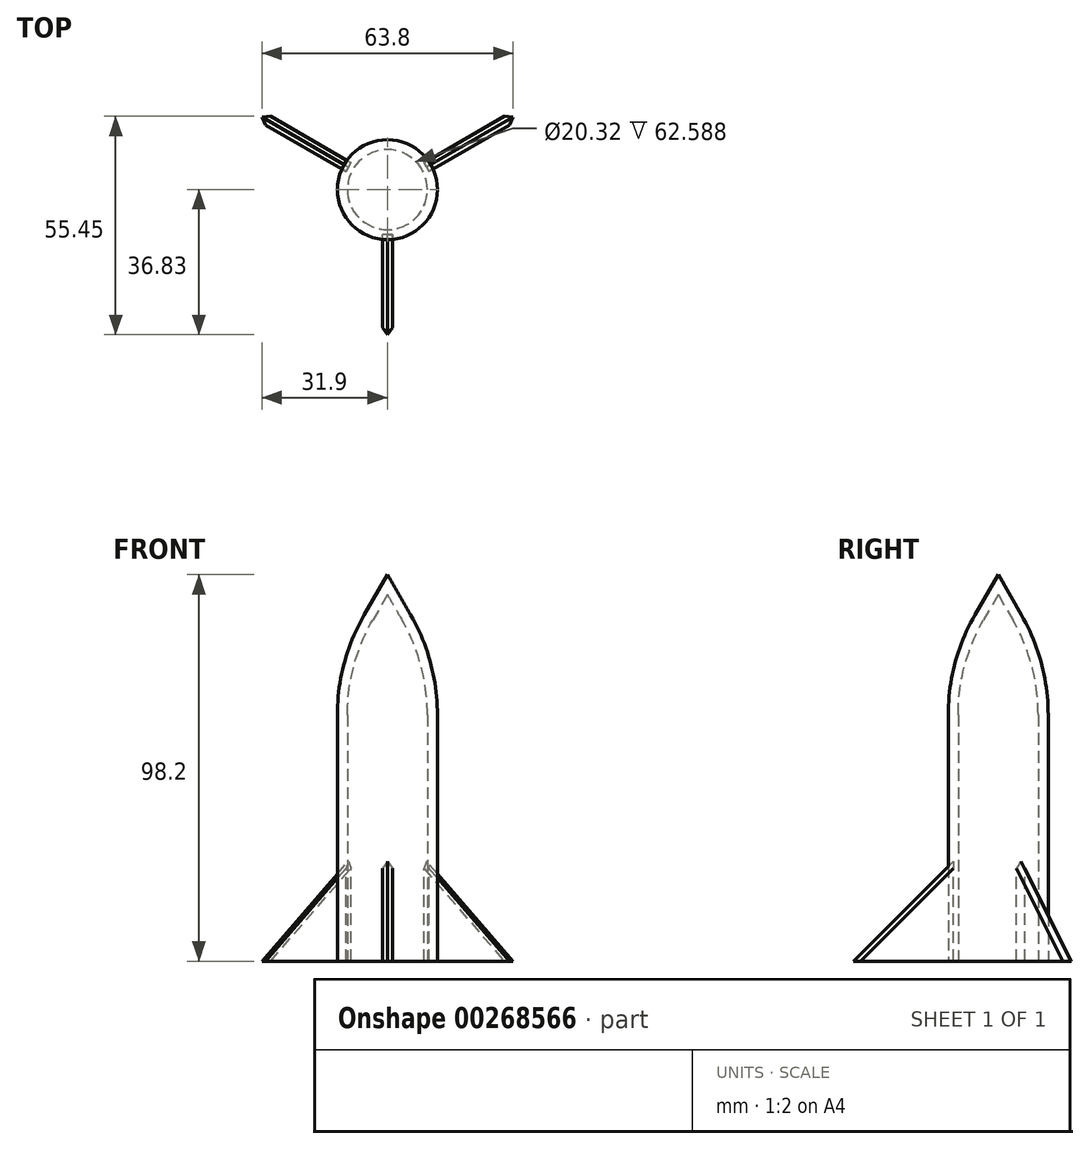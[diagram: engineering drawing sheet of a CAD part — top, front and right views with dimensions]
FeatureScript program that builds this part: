
annotation { "Feature Type Name" : "Feature", "Feature Type Description" : "" }
export const myFeature = defineFeature(function(context is Context, id is Id, definition is map)
    precondition{}
    {
        {
            var Q0;
            Q0=qCreatedBy(makeId("Top.planeOp"),FACE);
            var sketch = newSketch(context, id + "F0", { "sketchPlane" : qUnion([Q0])});
            skCircle(sketch, "E0", {"center": v(0, 0) * mm, "radius": 12.7 * mm});
            skSolve(sketch);
        }
        {
            var Q0;
            Q0 = qSketchRegion(id + "F0", true);
            extrude(context, id + "F1", {"entities" : qUnion([Q0]), "depth" : 76.2 * mm});
        }
        {
            var Q0;
            Q0=makeQuery(id+"F1.opExtrude","CAP_FACE",FACE,{"disambiguationData":[OSD([sQuery(id+"F0.wireOp",EDGE,"E0")])],"isStart":false});
            extrude(context, id + "F2", {"entities" : qUnion([Q0]), "operationType" : NewBodyOperationType.ADD, "depth" : 25.4 * mm, "hasDraft" : true, "draftAngle" : 30 * degree, "draftPullDirection" : true});
        }
        {
            var Q0;
            {var subQ0=sQuery(id+"F0.wireOp",EDGE,"E0");Q0=makeQuery(id+"F2.boolean.opBoolean","MERGE",EDGE,{"derivedFrom":[makeQuery(id+"F1.opExtrude","CAP_EDGE",EDGE,{"disambiguationData":[OSD([subQ0])],"isStart":false}),makeQuery(id+"F2.opExtrude","CAP_EDGE",EDGE,{"disambiguationData":[OSD([subQ0])],"isStart":true})]});}
            fillet(context, id + "F3", {"entities" : qUnion([Q0]), "radius" : 50.8 * mm, "tangentPropagation" : true, "allowEdgeOverflow" : false});
        }
        {
            var Q0;
            Q0=makeQuery(id+"F1.opExtrude","CAP_FACE",FACE,{"disambiguationData":[OSD([sQuery(id+"F0.wireOp",EDGE,"E0")])],"isStart":true});
            shell(context, id + "F4", {"entities" : qUnion([Q0]), "thickness" : 2.54 * mm});
        }
        {
            var Q0;
            Q0=qCreatedBy(makeId("Right.planeOp"),FACE);
            var sketch = newSketch(context, id + "F5", { "sketchPlane" : qUnion([Q0])});
            skLineSegment(sketch, "E1", {"start": v(-11.43, 0) * mm, "end": v(-11.43, 25.4) * mm});
            skLineSegment(sketch, "E2", {"start": v(-11.43, 25.4) * mm, "end": v(-36.83, 0) * mm});
            skLineSegment(sketch, "E3", {"start": v(-36.83, 0) * mm, "end": v(-11.43, 0) * mm});
            skSolve(sketch);
        }
        {
            var Q0;
            Q0 = qSketchRegion(id + "F5", true);
            extrude(context, id + "F6", {"entities" : qUnion([Q0]), "endBound" : BoundingType.SYMMETRIC, "depth" : 2.54 * mm});
        }
        {
            var Q0;
            Q0=makeQuery(id+"F6.opExtrude","CAP_EDGE",EDGE,{"disambiguationData":[OSD([sQuery(id+"F5.wireOp",EDGE,"E2")])],"isStart":false});
            var Q1;
            Q1=makeQuery(id+"F6.opExtrude","CAP_EDGE",EDGE,{"disambiguationData":[OSD([sQuery(id+"F5.wireOp",EDGE,"E2")])],"isStart":true});
            chamfer(context, id + "F7", {"entities" : qUnion([Q0, Q1]), "width" : 1.27 * mm, "tangentPropagation" : true});
        }
        {
            var Q0;
            Q0=makeQuery(id+"F6.opExtrude","SWEPT_BODY",BODY,{"disambiguationData":[OSD([sQuery(id+"F5.wireOp",EDGE,"E1"),sQuery(id+"F5.wireOp",EDGE,"E2"),sQuery(id+"F5.wireOp",EDGE,"E3")])]});
            var Q1;
            {var subQ0=sQuery(id+"F0.wireOp",EDGE,"E0");Q1=makeQuery(id+"F4.opShell","OFFSET_EDGE",EDGE,{"disambiguationData":[OSD([subQ0]),TDD([makeQuery(id+"F1.opExtrude","CAP_EDGE",EDGE,{"disambiguationData":[OSD([subQ0])],"isStart":true})])]});}
            circularPattern(context, id + "F8", {"entities" : qUnion([Q0]), "axis" : qUnion([Q1]), "angle" : 360 * degree, "instanceCount" : 3, "equalSpace" : true});
        }
    });
